# Revit family: Furniture-Grohe-Essentials-Holder-12-METRIC
name_source: partatom
category: Furniture
revit_build: Autodesk Revit Architecture 2012 (Build: 20110309_2315(x64)
units: mm (PartAtom-declared; Revit-internal decimal feet)

## types (2) — shared parameters
ADA Compliant = No
Assembly Code = C1030220
AssetType = Fixed
Default Elevation = 600 mm
Description = Essentials Holder
Ecojoy = No
Height = 28 mm  [stored 0.0918635 ft]
Keynote = N13
Length = 42 mm  [stored 0.137795 ft]
MaintenanceInformation = http://projects.grohe.com
Manufacturer = Grohe AG
Model = Essentials Holder 40369 000
ModelNumber = Essentials Holder 40369 000
Name = Essentials Holder 40369 000
Product Documentation Link = http://projects.grohe.com
Product Page URL = http://projects.grohe.com
Type Comments = Essentials Holder
URL = www.grohe.com
Width = 35 mm  [stored 0.114829 ft]
_current revision = 1
_distributed by = www.bimstore.co.uk
zero-valued in all types: Barcode, Cost, ExpectedLife, SerialNumber, TagNumber, _BIMspec_GUID

## per-type parameters (varying)
| type | Material |
| 40 369 000 - Chrome | Grohe-Chrome |
| 40 369 EN0 - Brushed Nickel | Grohe-Brushed_Nickel |

note: [stored X ft] marks values corroborated as IEEE doubles in the binary element streams (Revit-internal decimal feet)

## geometry (parser evidence)
native form markers: Blend x8, Sweep x1
no freeform markers — native parametric forms only
